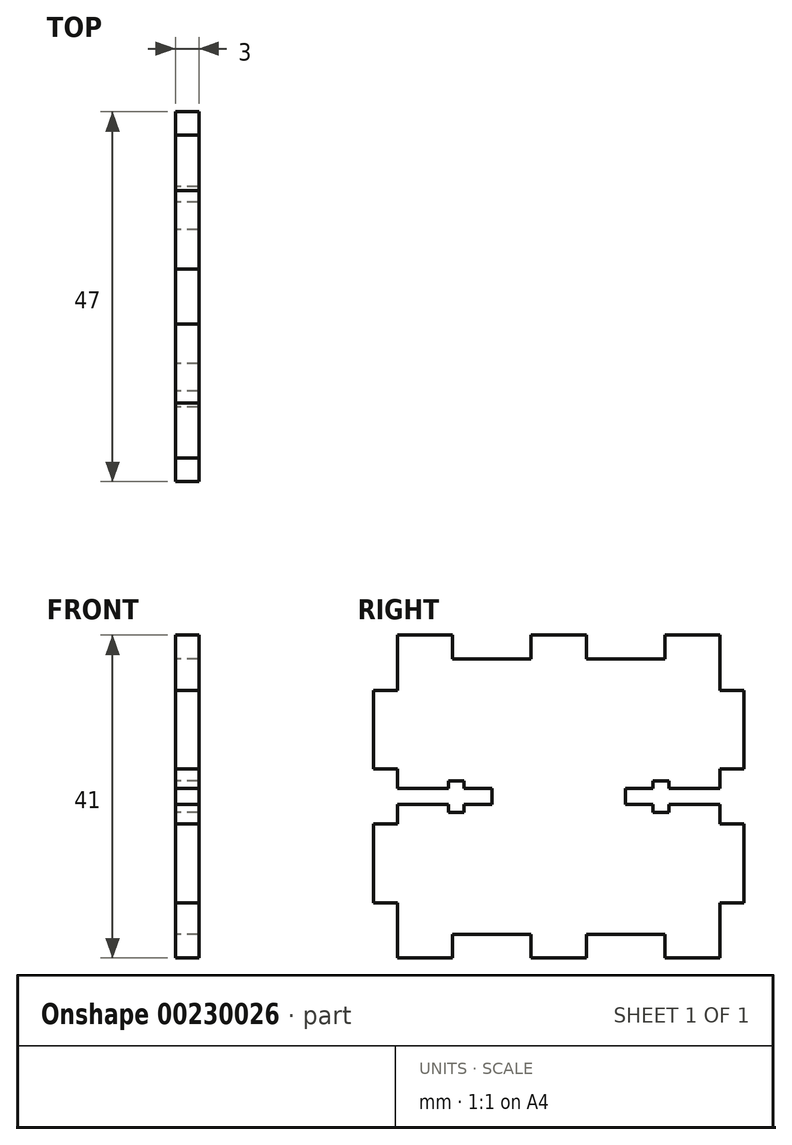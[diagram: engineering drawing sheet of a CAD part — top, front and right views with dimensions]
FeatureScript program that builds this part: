
annotation { "Feature Type Name" : "Feature", "Feature Type Description" : "" }
export const myFeature = defineFeature(function(context is Context, id is Id, definition is map)
    precondition{}
    {
        {
            var Q0;
            Q0=qCreatedBy(makeId("Right.planeOp"),FACE);
            var sketch = newSketch(context, id + "F0", { "sketchPlane" : qUnion([Q0])});
            skLineSegment(sketch, "E0", {"start": v(24, 0) * mm, "end": v(24, 3) * mm});
            skLineSegment(sketch, "E1", {"start": v(24, 3) * mm, "end": v(34, 3) * mm});
            skLineSegment(sketch, "E2", {"start": v(41, 7) * mm, "end": v(44, 7) * mm});
            skLineSegment(sketch, "E3", {"start": v(44, 7) * mm, "end": v(44, 17) * mm});
            skLineSegment(sketch, "E4", {"start": v(44, 17) * mm, "end": v(41, 17) * mm});
            skLineSegment(sketch, "E5", {"start": v(41, 17) * mm, "end": v(41, 19.5) * mm});
            skLineSegment(sketch, "E6", {"start": v(41, 19.5) * mm, "end": v(34.5, 19.5) * mm});
            skLineSegment(sketch, "E7", {"start": v(34.5, 19.5) * mm, "end": v(34.5, 18.5) * mm});
            skLineSegment(sketch, "E8", {"start": v(34.5, 18.5) * mm, "end": v(32.5, 18.5) * mm});
            skLineSegment(sketch, "E9", {"start": v(32.5, 18.5) * mm, "end": v(32.5, 19.5) * mm});
            skLineSegment(sketch, "E10", {"start": v(32.5, 19.5) * mm, "end": v(29, 19.5) * mm});
            skLineSegment(sketch, "E11", {"start": v(29, 19.5) * mm, "end": v(29, 20.5) * mm});
            skLineSegment(sketch, "E12", {"start": v(44.49, 20.5) * mm, "end": v(0, 20.5) * mm, "construction": true});
            skLineSegment(sketch, "E13", {"start": v(20.5, 0) * mm, "end": v(24, 0) * mm});
            skLineSegment(sketch, "E14", {"start": v(20.5, 41) * mm, "end": v(20.5, 0) * mm, "construction": true});
            skLineSegment(sketch, "E15", {"start": v(34, 3) * mm, "end": v(34, 0) * mm});
            skLineSegment(sketch, "E16", {"start": v(34, 0) * mm, "end": v(41, 0) * mm});
            skLineSegment(sketch, "E17", {"start": v(41, 0) * mm, "end": v(41, 7) * mm});
            skLineSegment(sketch, "E18.MirrorCS", {"start": v(34.5, 22.5) * mm, "end": v(32.5, 22.5) * mm});
            skLineSegment(sketch, "E19.MirrorCS", {"start": v(41, 34) * mm, "end": v(44, 34) * mm});
            skLineSegment(sketch, "E20.MirrorCS", {"start": v(29, 21.5) * mm, "end": v(29, 20.5) * mm});
            skLineSegment(sketch, "E21.MirrorCS", {"start": v(41, 24) * mm, "end": v(41, 21.5) * mm});
            skLineSegment(sketch, "E22.MirrorCS", {"start": v(32.5, 22.5) * mm, "end": v(32.5, 21.5) * mm});
            skLineSegment(sketch, "E23.MirrorCS", {"start": v(44, 24) * mm, "end": v(41, 24) * mm});
            skLineSegment(sketch, "E24.MirrorCS", {"start": v(34.5, 21.5) * mm, "end": v(34.5, 22.5) * mm});
            skLineSegment(sketch, "E25.MirrorCS", {"start": v(34, 41) * mm, "end": v(41, 41) * mm});
            skLineSegment(sketch, "E26.MirrorCS", {"start": v(41, 21.5) * mm, "end": v(34.5, 21.5) * mm});
            skLineSegment(sketch, "E27.MirrorCS", {"start": v(41, 41) * mm, "end": v(41, 34) * mm});
            skLineSegment(sketch, "E28.MirrorCS", {"start": v(32.5, 21.5) * mm, "end": v(29, 21.5) * mm});
            skLineSegment(sketch, "E29.MirrorCS", {"start": v(24, 41) * mm, "end": v(24, 38) * mm});
            skLineSegment(sketch, "E30.MirrorCS", {"start": v(24, 38) * mm, "end": v(34, 38) * mm});
            skLineSegment(sketch, "E31.MirrorCS", {"start": v(44, 34) * mm, "end": v(44, 24) * mm});
            skLineSegment(sketch, "E32.MirrorCS", {"start": v(20.5, 41) * mm, "end": v(24, 41) * mm});
            skLineSegment(sketch, "E33.MirrorCS", {"start": v(34, 38) * mm, "end": v(34, 41) * mm});
            skLineSegment(sketch, "E34.MirrorCS", {"start": v(12, 21.5) * mm, "end": v(12, 20.5) * mm});
            skLineSegment(sketch, "E35.MirrorCS", {"start": v(6.5, 19.5) * mm, "end": v(6.5, 18.5) * mm});
            skLineSegment(sketch, "E36.MirrorCS", {"start": v(12, 19.5) * mm, "end": v(12, 20.5) * mm});
            skLineSegment(sketch, "E37.MirrorCS", {"start": v(6.5, 22.5) * mm, "end": v(8.5, 22.5) * mm});
            skLineSegment(sketch, "E38.MirrorCS", {"start": v(6.5, 21.5) * mm, "end": v(6.5, 22.5) * mm});
            skLineSegment(sketch, "E39.MirrorCS", {"start": v(8.5, 21.5) * mm, "end": v(12, 21.5) * mm});
            skLineSegment(sketch, "E40.MirrorCS", {"start": v(8.5, 18.5) * mm, "end": v(8.5, 19.5) * mm});
            skLineSegment(sketch, "E41.MirrorCS", {"start": v(6.5, 18.5) * mm, "end": v(8.5, 18.5) * mm});
            skLineSegment(sketch, "E42.MirrorCS", {"start": v(8.5, 19.5) * mm, "end": v(12, 19.5) * mm});
            skLineSegment(sketch, "E43.MirrorCS", {"start": v(20.5, 0) * mm, "end": v(17, 0) * mm});
            skLineSegment(sketch, "E44.MirrorCS", {"start": v(7, 3) * mm, "end": v(7, 0) * mm});
            skLineSegment(sketch, "E45.MirrorCS", {"start": v(0, 7) * mm, "end": v(-3, 7) * mm});
            skLineSegment(sketch, "E46.MirrorCS", {"start": v(0, 17) * mm, "end": v(0, 19.5) * mm});
            skLineSegment(sketch, "E47.MirrorCS", {"start": v(7, 38) * mm, "end": v(7, 41) * mm});
            skLineSegment(sketch, "E48.MirrorCS", {"start": v(8.5, 22.5) * mm, "end": v(8.5, 21.5) * mm});
            skLineSegment(sketch, "E49.MirrorCS", {"start": v(0, 34) * mm, "end": v(-3, 34) * mm});
            skLineSegment(sketch, "E50.MirrorCS", {"start": v(17, 0) * mm, "end": v(17, 3) * mm});
            skLineSegment(sketch, "E51.MirrorCS", {"start": v(20.5, 41) * mm, "end": v(17, 41) * mm});
            skLineSegment(sketch, "E52.MirrorCS", {"start": v(17, 41) * mm, "end": v(17, 38) * mm});
            skLineSegment(sketch, "E53.MirrorCS", {"start": v(0, 24) * mm, "end": v(0, 21.5) * mm});
            skLineSegment(sketch, "E54.MirrorCS", {"start": v(-3, 24) * mm, "end": v(0, 24) * mm});
            skLineSegment(sketch, "E55.MirrorCS", {"start": v(-3, 17) * mm, "end": v(0, 17) * mm});
            skLineSegment(sketch, "E56.MirrorCS", {"start": v(-3, 34) * mm, "end": v(-3, 24) * mm});
            skLineSegment(sketch, "E57.MirrorCS", {"start": v(17, 38) * mm, "end": v(7, 38) * mm});
            skLineSegment(sketch, "E58.MirrorCS", {"start": v(7, 41) * mm, "end": v(0, 41) * mm});
            skLineSegment(sketch, "E59.MirrorCS", {"start": v(0, 19.5) * mm, "end": v(6.5, 19.5) * mm});
            skLineSegment(sketch, "E60.MirrorCS", {"start": v(0, 21.5) * mm, "end": v(6.5, 21.5) * mm});
            skLineSegment(sketch, "E61.MirrorCS", {"start": v(17, 3) * mm, "end": v(7, 3) * mm});
            skLineSegment(sketch, "E62.MirrorCS", {"start": v(0, 0) * mm, "end": v(0, 7) * mm});
            skLineSegment(sketch, "E63.MirrorCS", {"start": v(7, 0) * mm, "end": v(0, 0) * mm});
            skLineSegment(sketch, "E64.MirrorCS", {"start": v(0, 41) * mm, "end": v(0, 34) * mm});
            skLineSegment(sketch, "E65.MirrorCS", {"start": v(-3, 7) * mm, "end": v(-3, 17) * mm});
            skSolve(sketch);
        }
        {
            var Q0;
            Q0 = qSketchRegion(id + "F0", true);
            extrude(context, id + "F1", {"entities" : qUnion([Q0]), "depth" : 3 * mm});
        }
    });
